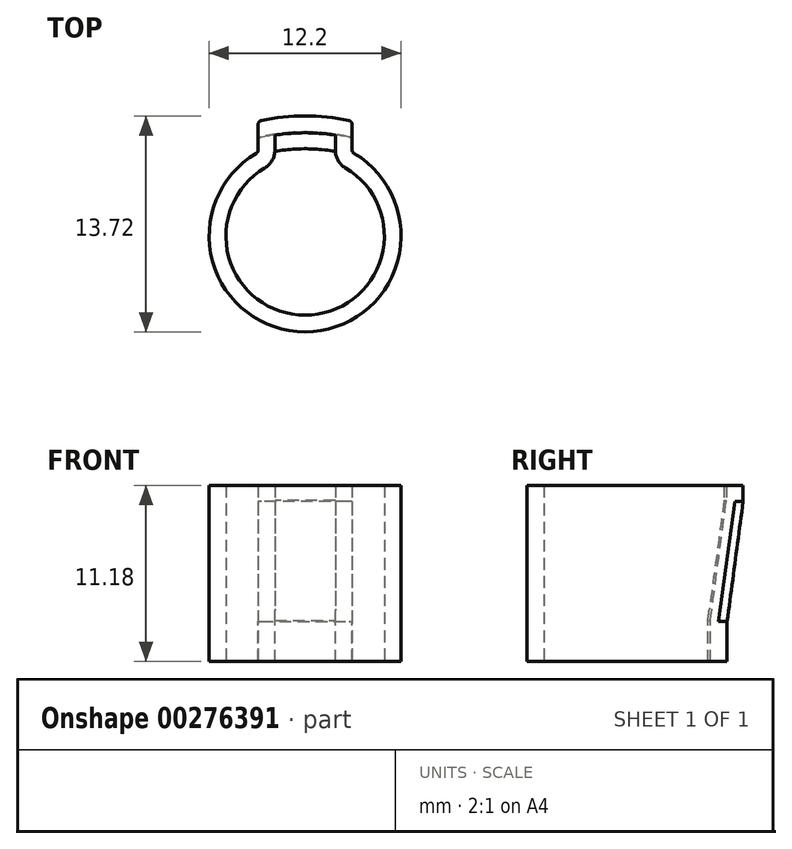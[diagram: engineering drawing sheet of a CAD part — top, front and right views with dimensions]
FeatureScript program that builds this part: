
annotation { "Feature Type Name" : "Feature", "Feature Type Description" : "" }
export const myFeature = defineFeature(function(context is Context, id is Id, definition is map)
    precondition{}
    {
        {
            var Q0;
            Q0=qCreatedBy(makeId("Top.planeOp"),FACE);
            var sketch = newSketch(context, id + "F0", { "sketchPlane" : qUnion([Q0])});
            skArc(sketch, "E0", {"start": v(-3.1, 5.24) * mm, "mid": v(0, -6.1) * mm, "end": v(3.1, 5.24) * mm});
            skLineSegment(sketch, "E1", {"start": v(0, -6.1) * mm, "end": v(0, 7.62) * mm, "construction": true});
            skArc(sketch, "E2", {"start": v(2.78, 7.33) * mm, "mid": v(0, 7.62) * mm, "end": v(-2.78, 7.33) * mm});
            skLineSegment(sketch, "E3", {"start": v(-2.98, 5.46) * mm, "end": v(-2.98, 7.09) * mm});
            skLineSegment(sketch, "E4", {"start": v(2.98, 7.09) * mm, "end": v(2.98, 5.46) * mm});
            skPoint(sketch, "E5.visualSharp", {"position": v(2.98, 7.3) * mm});
            skArc(sketch, "E5.filletArc", {"start": v(2.98, 7.09) * mm, "mid": v(2.93, 7.25) * mm, "end": v(2.78, 7.33) * mm});
            skPoint(sketch, "E6.visualSharp", {"position": v(-2.98, 7.3) * mm});
            skArc(sketch, "E6.filletArc", {"start": v(-2.78, 7.33) * mm, "mid": v(-2.93, 7.25) * mm, "end": v(-2.98, 7.09) * mm});
            skPoint(sketch, "E7.visualSharp", {"position": v(-2.98, 5.32) * mm});
            skArc(sketch, "E7.filletArc", {"start": v(-3.1, 5.24) * mm, "mid": v(-3.02, 5.34) * mm, "end": v(-2.98, 5.46) * mm});
            skPoint(sketch, "E8.visualSharp", {"position": v(2.98, 5.32) * mm});
            skArc(sketch, "E8.filletArc", {"start": v(2.98, 5.46) * mm, "mid": v(3.02, 5.34) * mm, "end": v(3.1, 5.24) * mm});
            skSolve(sketch);
        }
        {
            var Q0;
            Q0 = qSketchRegion(id + "F0", true);
            extrude(context, id + "F1", {"entities" : qUnion([Q0]), "depth" : 1.02 * mm});
        }
        {
            var Q0;
            Q0=makeQuery(id+"F1.opExtrude","CAP_FACE",FACE,{"disambiguationData":[OSD([sQuery(id+"F0.wireOp",EDGE,"E0"),sQuery(id+"F0.wireOp",EDGE,"E2"),sQuery(id+"F0.wireOp",EDGE,"E3"),sQuery(id+"F0.wireOp",EDGE,"E4"),sQuery(id+"F0.wireOp",EDGE,"E5.filletArc"),sQuery(id+"F0.wireOp",EDGE,"E6.filletArc"),sQuery(id+"F0.wireOp",EDGE,"E7.filletArc"),sQuery(id+"F0.wireOp",EDGE,"E8.filletArc")])],"isStart":true});
            cPlane(context, id + "F2", {"entities" : qUnion([Q0]), "cplaneType" : CPlaneType.OFFSET, "offset" : 7.62 * mm, "width" : 152.4 * mm, "height" : 152.4 * mm});
        }
        {
            var Q0;
            Q0=qCreatedBy(id+"F2.planeOp",FACE);
            var sketch = newSketch(context, id + "F3", { "sketchPlane" : qUnion([Q0])});
            skArc(sketch, "E9", {"start": v(3.1, -5.24) * mm, "mid": v(0, 6.1) * mm, "end": v(-3.1, -5.24) * mm});
            skLineSegment(sketch, "E10", {"start": v(0, 6.1) * mm, "end": v(0, -6.6) * mm, "construction": true});
            skArc(sketch, "E11", {"start": v(-2.79, -6.3) * mm, "mid": v(0, -6.6) * mm, "end": v(2.79, -6.3) * mm});
            skLineSegment(sketch, "E12", {"start": v(2.98, -5.46) * mm, "end": v(2.98, -6.05) * mm});
            skLineSegment(sketch, "E13", {"start": v(-2.98, -6.05) * mm, "end": v(-2.98, -5.46) * mm});
            skPoint(sketch, "E14.visualSharp", {"position": v(-2.98, -6.25) * mm});
            skArc(sketch, "E14.filletArc", {"start": v(-2.98, -6.05) * mm, "mid": v(-2.93, -6.2) * mm, "end": v(-2.79, -6.3) * mm});
            skPoint(sketch, "E15.visualSharp", {"position": v(2.98, -6.25) * mm});
            skArc(sketch, "E15.filletArc", {"start": v(2.79, -6.3) * mm, "mid": v(2.93, -6.2) * mm, "end": v(2.98, -6.05) * mm});
            skPoint(sketch, "E16.visualSharp", {"position": v(2.98, -5.32) * mm});
            skArc(sketch, "E16.filletArc", {"start": v(3.1, -5.24) * mm, "mid": v(3.02, -5.34) * mm, "end": v(2.98, -5.46) * mm});
            skPoint(sketch, "E17.visualSharp", {"position": v(-2.98, -5.32) * mm});
            skArc(sketch, "E17.filletArc", {"start": v(-2.98, -5.46) * mm, "mid": v(-3.02, -5.34) * mm, "end": v(-3.1, -5.24) * mm});
            skSolve(sketch);
        }
        {
            var Q0;
            Q0 = qSketchRegion(id + "F3", true);
            extrude(context, id + "F4", {"entities" : qUnion([Q0]), "depth" : 2.54 * mm});
        }
        {
            var Q0;
            Q0=makeQuery(id+"F1.opExtrude","CAP_FACE",FACE,{"disambiguationData":[OSD([sQuery(id+"F0.wireOp",EDGE,"E0"),sQuery(id+"F0.wireOp",EDGE,"E2"),sQuery(id+"F0.wireOp",EDGE,"E3"),sQuery(id+"F0.wireOp",EDGE,"E4"),sQuery(id+"F0.wireOp",EDGE,"E5.filletArc"),sQuery(id+"F0.wireOp",EDGE,"E6.filletArc"),sQuery(id+"F0.wireOp",EDGE,"E7.filletArc"),sQuery(id+"F0.wireOp",EDGE,"E8.filletArc")])],"isStart":true});
            var Q1;
            Q1=makeQuery(id+"F4.opExtrude","CAP_FACE",FACE,{"disambiguationData":[OSD([sQuery(id+"F3.wireOp",EDGE,"E9"),sQuery(id+"F3.wireOp",EDGE,"E11"),sQuery(id+"F3.wireOp",EDGE,"E12"),sQuery(id+"F3.wireOp",EDGE,"E13"),sQuery(id+"F3.wireOp",EDGE,"E14.filletArc"),sQuery(id+"F3.wireOp",EDGE,"E15.filletArc"),sQuery(id+"F3.wireOp",EDGE,"E16.filletArc"),sQuery(id+"F3.wireOp",EDGE,"E17.filletArc")])],"isStart":true});
            loft(context, id + "F5", {"operationType" : NewBodyOperationType.ADD, "sheetProfilesArray" : [{ "sheetProfileEntities" : qUnion([Q0]) }, { "sheetProfileEntities" : qUnion([Q1]) }]});
        }
        {
            var Q0;
            Q0=makeQuery(id+"F1.opExtrude","CAP_FACE",FACE,{"disambiguationData":[OSD([sQuery(id+"F0.wireOp",EDGE,"E0"),sQuery(id+"F0.wireOp",EDGE,"E2"),sQuery(id+"F0.wireOp",EDGE,"E3"),sQuery(id+"F0.wireOp",EDGE,"E4"),sQuery(id+"F0.wireOp",EDGE,"E5.filletArc"),sQuery(id+"F0.wireOp",EDGE,"E6.filletArc"),sQuery(id+"F0.wireOp",EDGE,"E7.filletArc"),sQuery(id+"F0.wireOp",EDGE,"E8.filletArc")])],"isStart":false});
            var Q1;
            Q1=makeQuery(id+"F4.opExtrude","CAP_FACE",FACE,{"disambiguationData":[OSD([sQuery(id+"F3.wireOp",EDGE,"E9"),sQuery(id+"F3.wireOp",EDGE,"E11"),sQuery(id+"F3.wireOp",EDGE,"E12"),sQuery(id+"F3.wireOp",EDGE,"E13"),sQuery(id+"F3.wireOp",EDGE,"E14.filletArc"),sQuery(id+"F3.wireOp",EDGE,"E15.filletArc"),sQuery(id+"F3.wireOp",EDGE,"E16.filletArc"),sQuery(id+"F3.wireOp",EDGE,"E17.filletArc")])],"isStart":false});
            shell(context, id + "F6", {"entities" : qUnion([Q0, Q1]), "thickness" : 1.07 * mm});
        }
    });
